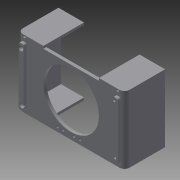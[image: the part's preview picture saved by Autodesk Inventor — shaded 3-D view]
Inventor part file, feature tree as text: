
AUTODESK INVENTOR PART (.ipt)
format: ipt  version: 2013 (Build 170138000, 138)  size: 293,888 bytes
history: native  units: in
note: dims shown in document units (in); Inventor stores cm internally (conversion verified against a paired STEP export)
features: extrude x8, sketch x6, reference x5, fillet x2, projected_geometry x2, chamfer x1
ambient origin geometry x8: Origin, YZ Plane, XZ Plane, XY Plane, X Axis, Y Axis, Z Axis, Center Point
bodies: Solid1 (feature_tree)
feature tree (24):
  extrude  "Extrusion1"  Depth=1.4961in TaperAngle=0.0deg
  extrude  "Extrusion2"  Depth=0.0394in TaperAngle=45.0deg
  extrude  "Extrusion3"  Depth=2.2047in
  chamfer  "Chamfer1"  Distance=3.937in
  extrude  "Extrusion4"  TaperAngle=0.0deg  [1 undecoded]
  fillet  "Fillet2"  Radius=0.1181in
  fillet  "Fillet3"  Radius=0.1181in
  extrude  "Extrusion5"  Depth=0.1575in
  extrude  "Extrusion6"  Depth=2.25in
  extrude  "Extrusion9"  Depth=4.0in
  extrude  "Extrusion10"  Depth=0.15in
  sketch  "Sketch2"  dims[d6=0.1181in d7=0.0in d9=1.4961in d10=0.0in]
  sketch  "Sketch4"  dims[d12=0.1181in d13=0.0in d15=0.0394in d16=0.0787in d17=45.0deg]
  reference  "Reference2"
  reference  "Reference3"
  reference  "Reference4"
  reference  "Reference5"
  sketch  "Sketch5"  dims[d28=2.2047in d29=2.2047in d31=3.937in d32=0.0in]
  projected_geometry  "Projected Loop1"
  reference  "Reference14"
  sketch  "Sketch6"  dims[d41=0.2756in d42=0.0in d43=0.1181in d44=0.1181in]
  sketch  "Sketch7"  dims[d45=0.1575in d46=0.1575in]
  sketch  "Sketch10"  dims[d47=2.25in d48=2.25in d49=4.0in d50=0.15in d51=0.0984in d52=0.0984in d53=0.0984in d54=0.0984in d56=2.6772in d59=2.2047in d60=0.1969in d61=0.1969in d62=0.0984in d63=0.0in d64=0.0787in d66=0.1181in d67=0.0394in d68=0.0394in d69=0.1575in d78=0.6496in d79=0.5122in d80=0.0587in d81=0.1181in d82=0.0in d101=0.1181in d103=0.1181in d104=0.1181in d105=0.1181in d106=0.0787in d107=0.0787in d108=0.1181in d109=0.0787in d110=0.0in d111=0.0in d112=0.1969in d114=0.1969in d115=0.1969in d116=0.1969in d117=0.1181in d118=0.0in]
  projected_geometry  "Projected Loop2"
note: 1 required parameter value undecoded (feature->parameter linkage not recoverable at this tier; creation-order binding heuristic only, values carry confidence <= 0.55)
